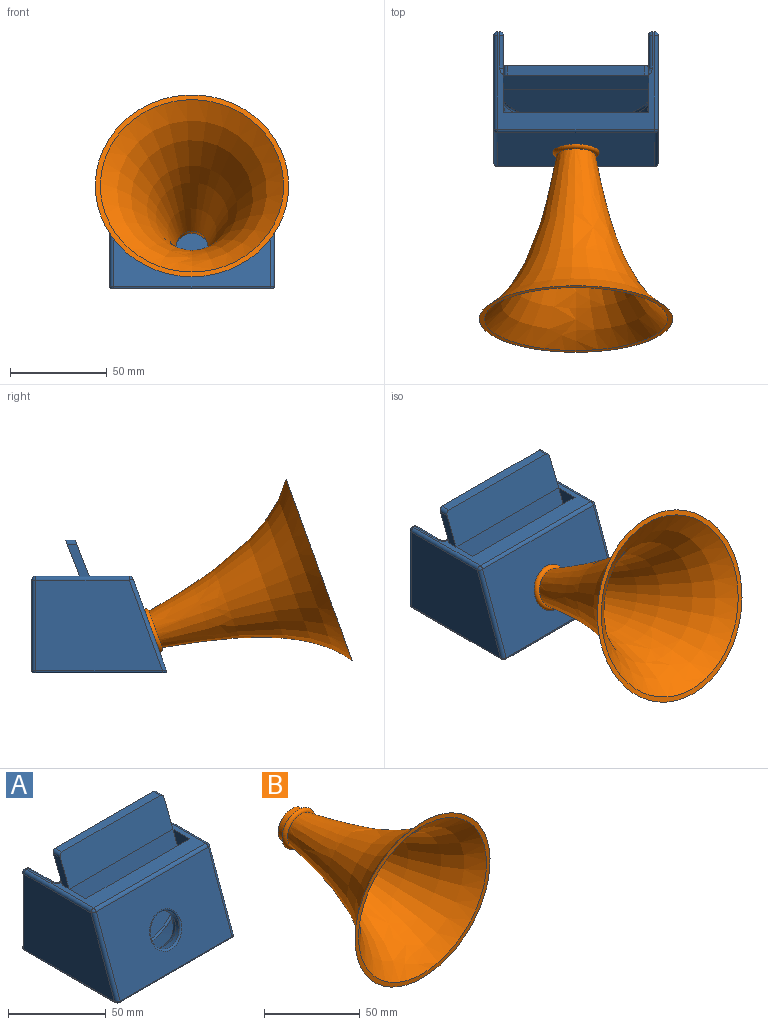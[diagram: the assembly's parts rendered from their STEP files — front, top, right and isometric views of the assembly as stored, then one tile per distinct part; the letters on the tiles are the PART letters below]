
ASSEMBLY  parts=2 mates=1
PART A: 76 faces, bbox 86x70.4x69.3 mm
  f0: plane 47x0.99mm, normal (0,1,0), area 46.7mm2, adj f51,f54,f57,f65
  f1: plane 83.64x68.21mm, normal (0,0,-1), area 4011.8mm2, adj f60,f61,f62,f63,f64,f65,f66,f67
  f2: plane 81x48.4mm, normal (0,0,1), area 1011.6mm2, adj f11,f12,f14,f28,f29,f30,f35,f40
  f3: torus R=37.83mm, axis (0,-0.94,0.34), area 57.1mm2, adj f10,f11,f16,f17,f18,f23
  f4: torus R=37.83mm, axis (0,-0.94,0.34), area 57.1mm2, adj f5,f11,f16,f17,f18,f21
  f5: plane 12.08x1.47mm, normal (0,0,1), area 7.8mm2, adj f4,f11,f13,f14,f18,f24
  f6: plane 81x47.34mm, normal (0,-0.94,0.34), area 3700.7mm2, adj f25,f42,f47,f48,f62
  f7: plane 47x1mm, normal (0,1,0), area 47mm2, adj f34,f35,f36,f70
  f8: plane 65.51x47mm, normal (1,0,0), area 2676.9mm2, adj f36,f41,f42,f66
  f9: plane 65.51x47mm, normal (-1,0,0), area 2676.9mm2, adj f48,f53,f54,f61
  f10: plane 12.08x1.47mm, normal (0,0,1), area 7.8mm2, adj f3,f11,f12,f13,f18,f24
  f11: plane 75x18.79mm, normal (0,0.94,-0.34), area 1197.7mm2, adj f2,f3,f4,f5,f10,f12,f14,f16
  f12: plane 18.84x18.79mm, normal (1,0,0), area 225.5mm2, adj f2,f10,f11,f13
  f13: plane 75.01x44.88mm, normal (0,-0.94,0.34), area 2995.6mm2, adj f5,f10,f12,f14,f24,f27
  f14: plane 18.84x18.79mm, normal (-1,0,0), area 225.5mm2, adj f2,f5,f11,f13
  f15: cylinder r=10mm len=20.29mm, axis (0,-0.94,0.34), area 183.1mm2, adj f19,f20,f25
  f16: plane 74.99x0.75mm, normal (0,-0.34,-0.94), area 53.8mm2, adj f3,f4,f11,f17
  f17: plane 72.93x24.04mm, normal (0,0.94,-0.34), area 875.3mm2, adj f3,f4,f16,f19
  f18: cylinder r=38.83mm len=74.8mm, axis (0,0.94,-0.34), area 973.2mm2, adj f3,f4,f5,f10,f21,f22,f23,f24
  f19: torus R=15mm, axis (0,-0.94,0.34), area 416.4mm2, adj f15,f17,f20,f21,f23
  f20: bspline ~24.7x6.79mm, area 84.6mm2, adj f15,f19,f22
  f21: bspline ~4.32x2.31mm, area 3mm2, adj f4,f18,f19,f22
  f22: bspline ~23.09x2.68mm, area 20.5mm2, adj f18,f20,f21,f23
  f23: bspline ~5.4x2.75mm, area 3mm2, adj f3,f18,f19,f22
  f24: torus R=37.83mm, axis (0,0.94,-0.34), area 157.4mm2, adj f5,f10,f13,f18
  f25: torus R=11mm, axis (0,-0.94,0.34), area 102.3mm2, adj f6,f15
  f26: plane 71.01x5mm, normal (0,0,1), area 355mm2, adj f27,f29,f58,f59
  f27: plane 75.34x18.95mm, normal (0,-0.93,0.37), area 1498.3mm2, adj f13,f26,f28,f30,f58,f59
  f28: plane 16.62x11.52mm, normal (1,0,0), area 83.1mm2, adj f2,f27,f29,f59
  f29: plane 75.34x18.95mm, normal (0,0.93,-0.37), area 1498.3mm2, adj f2,f26,f28,f30,f58,f59
  f30: plane 16.62x11.52mm, normal (-1,0,0), area 83.1mm2, adj f2,f27,f29,f58
  f31: plane 47x16.77mm, normal (1,0,0), area 788mm2, adj f45,f51,f52,f69
  f32: plane 71.01x47mm, normal (0,1,0), area 3337.3mm2, adj f39,f45,f46,f73
  f33: plane 47x16.77mm, normal (-1,0,0), area 788mm2, adj f34,f39,f40,f74
  f34: cylinder r=2mm len=47mm, axis (0,0,1), area 147.7mm2, adj f7,f33,f37,f72
  f35: cylinder r=2mm len=2mm, axis (-1,0,0), area 3.1mm2, adj f2,f7,f37,f38
  f36: cylinder r=2mm len=47mm, axis (0,0,-1), area 147.7mm2, adj f7,f8,f38,f68
  f37: sphere r=2mm, area 8.6mm2, adj f34,f35,f40
  f38: sphere r=2mm, area 4mm2, adj f35,f36,f41
  f39: cylinder r=2mm len=47mm, axis (0,0,-1), area 147.7mm2, adj f32,f33,f43,f75
  f40: cylinder r=2mm len=16.77mm, axis (0,1,0), area 52.7mm2, adj f2,f33,f37,f43
  f41: cylinder r=2mm len=48.4mm, axis (0,1,0), area 152.1mm2, adj f2,f8,f38,f44
  f42: cylinder r=2mm len=48.03mm, axis (0,0.34,0.94), area 157.7mm2, adj f6,f8,f44,f64
  f43: torus R=4mm, axis (0,0,-1), area 13.5mm2, adj f2,f39,f40,f46
  f44: sphere r=2mm, area 5.2mm2, adj f41,f42,f47
  f45: cylinder r=2mm len=47mm, axis (0,0,1), area 147.7mm2, adj f31,f32,f49,f71
  f46: cylinder r=2mm len=71.01mm, axis (1,0,0), area 223.1mm2, adj f2,f32,f43,f49
  f47: cylinder r=2mm len=81mm, axis (1,0,0), area 197.9mm2, adj f2,f6,f44,f50
  f48: cylinder r=2mm len=48.03mm, axis (0,-0.34,-0.94), area 157.7mm2, adj f6,f9,f50,f60
  f49: torus R=4mm, axis (0,0,-1), area 13.5mm2, adj f2,f45,f46,f52
  f50: sphere r=2mm, area 5.2mm2, adj f47,f48,f53
  f51: cylinder r=2mm len=47mm, axis (0,0,-1), area 147.7mm2, adj f0,f31,f55,f67
  f52: cylinder r=2mm len=16.77mm, axis (0,-1,0), area 52.7mm2, adj f2,f31,f49,f55
  f53: cylinder r=2mm len=48.4mm, axis (0,-1,0), area 152.1mm2, adj f2,f9,f50,f56
  f54: cylinder r=2mm len=47mm, axis (0,0,1), area 147.7mm2, adj f0,f9,f56,f63
  f55: sphere r=2mm, area 8.6mm2, adj f51,f52,f57
  f56: sphere r=2mm, area 8.6mm2, adj f53,f54,f57
  f57: cylinder r=2mm len=2mm, axis (-1,0,0), area 3.1mm2, adj f0,f2,f55,f56
  f58: cylinder r=2mm len=5.79mm, axis (0,-1,0), area 15.7mm2, adj f26,f27,f29,f30
  f59: cylinder r=2mm len=5.79mm, axis (0,1,0), area 15.7mm2, adj f26,f27,f28,f29
  f60: bspline ~2.06x2mm, area 4.8mm2, adj f1,f48,f61,f62
  f61: cylinder r=1mm len=65.51mm, axis (0,1,0), area 102.9mm2, adj f1,f9,f60,f63
  f62: cylinder r=1mm len=81mm, axis (1,0,0), area 155.5mm2, adj f1,f6,f60,f64
  f63: torus R=1mm, axis (0,0,1), area 4mm2, adj f1,f54,f61,f65
  f64: bspline ~2.06x2mm, area 4.8mm2, adj f1,f42,f62,f66
  f65: cylinder r=1mm len=1mm, axis (-1,0,0), area 1.6mm2, adj f0,f1,f63,f67
  f66: cylinder r=1mm len=65.51mm, axis (0,-1,0), area 102.9mm2, adj f1,f8,f64,f68
  f67: torus R=1mm, axis (0,0,1), area 4mm2, adj f1,f51,f65,f69
  f68: torus R=1mm, axis (0,0,1), area 4mm2, adj f1,f36,f66,f70
  f69: cylinder r=1mm len=16.77mm, axis (0,1,0), area 26.3mm2, adj f1,f31,f67,f71
  f70: cylinder r=1mm len=1mm, axis (-1,0,0), area 1.6mm2, adj f1,f7,f68,f72
  f71: torus R=3mm, axis (0,0,1), area 5.8mm2, adj f1,f45,f69,f73
  f72: torus R=1mm, axis (0,0,1), area 4mm2, adj f1,f34,f70,f74
  f73: cylinder r=1mm len=71.01mm, axis (-1,0,0), area 111.5mm2, adj f1,f32,f71,f75
  f74: cylinder r=1mm len=16.77mm, axis (0,-1,0), area 26.3mm2, adj f1,f33,f72,f75
  f75: torus R=3mm, axis (0,0,1), area 5.8mm2, adj f1,f39,f73,f74
PART B: 9 faces, bbox 100x97.1x100 mm
  f0: plane 100x100mm, normal (0,-1,0), area 808mm2, adj f3,f6
  f1: cylinder r=10mm len=20mm, axis (0,-1,0), area 314.2mm2, adj f2,f7
  f2: plane 24x24mm, normal (0,1,0), area 138.2mm2, adj f1,f8
  f3: revolved ~100x100mm, area 15642.9mm2, adj f0,f8
  f4: plane 17x17mm, normal (0,1,0), area 15.7mm2, adj f5,f6
  f5: cylinder r=8.5mm len=17mm, axis (0,-1,0), area 190.3mm2, adj f4,f7
  f6: revolved ~94.72x94.72mm, area 14460.7mm2, adj f0,f4
  f7: torus R=10.5mm, axis (0,1,0), area 149.6mm2, adj f1,f5
  f8: torus R=10mm, axis (0,-1,0), area 222.5mm2, adj f2,f3
PLACE A t=(-21,72.57,44.13)mm
PLACE B rot(axis=(-1,0,0),20deg) t=(-21,-40.94,97.41)mm
MATE fastened B.f1 <-> A.f19  axis (0,0.94,-0.34) through (-21,45.51,65.94)mm
